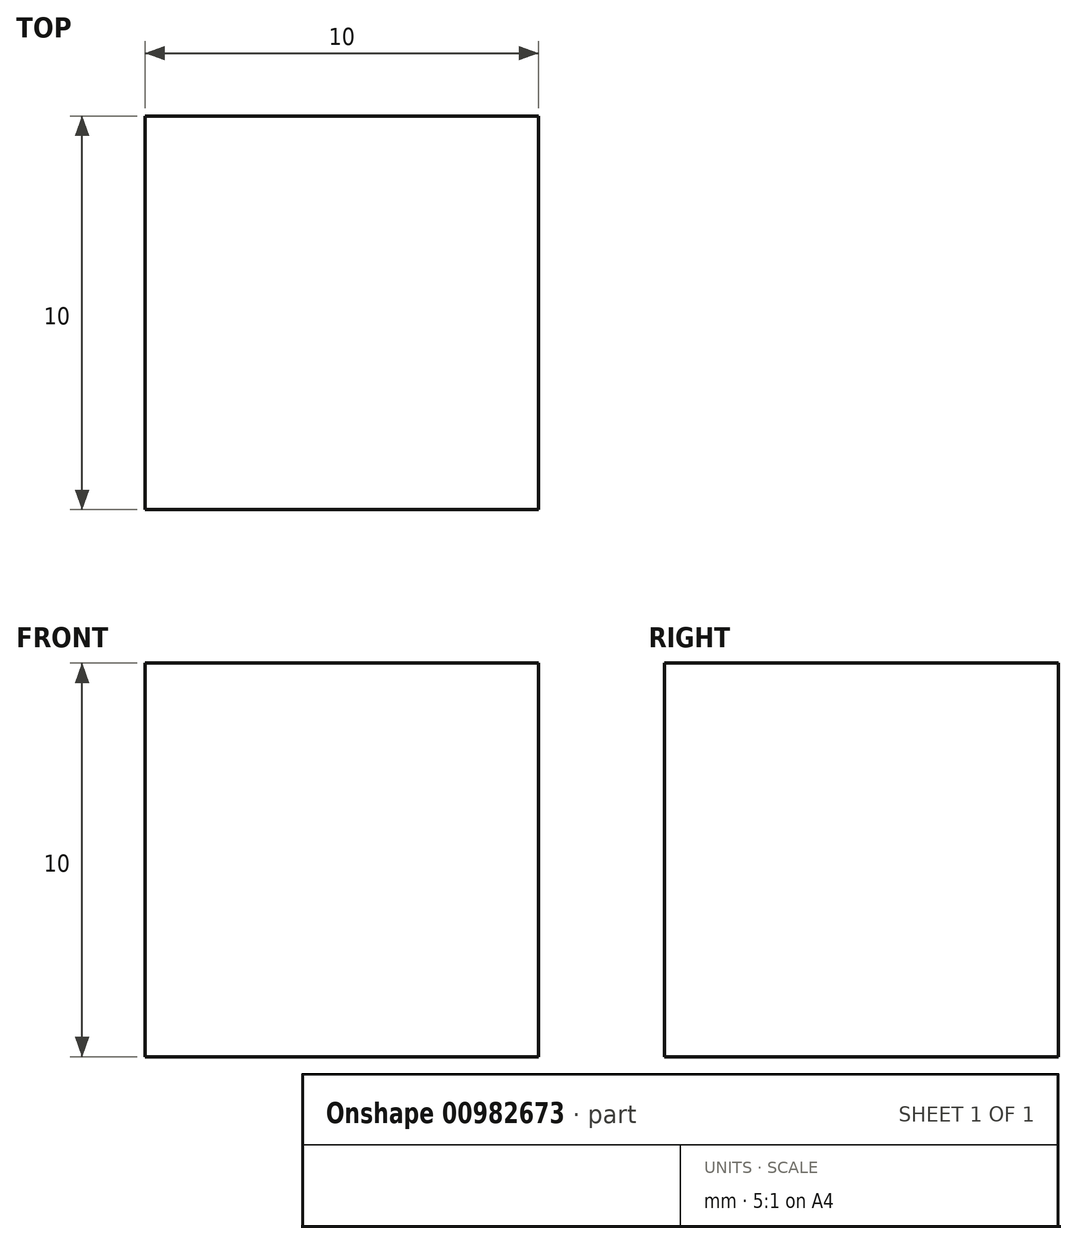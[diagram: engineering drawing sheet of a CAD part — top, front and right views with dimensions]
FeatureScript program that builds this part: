
annotation { "Feature Type Name" : "Feature", "Feature Type Description" : "" }
export const myFeature = defineFeature(function(context is Context, id is Id, definition is map)
    precondition{}
    {
        {
            var Q0;
            Q0=qCreatedBy(makeId("Front.planeOp"),FACE);
            var sketch = newSketch(context, id + "F0", { "sketchPlane" : qUnion([Q0])});
            skLineSegment(sketch, "E0.bottom", {"start": v(0, 0) * mm, "end": v(10, 0) * mm});
            skLineSegment(sketch, "E0.top", {"start": v(0, -10) * mm, "end": v(10, -10) * mm});
            skLineSegment(sketch, "E0.left", {"start": v(0, 0) * mm, "end": v(0, -10) * mm});
            skLineSegment(sketch, "E0.right", {"start": v(10, 0) * mm, "end": v(10, -10) * mm});
            skSolve(sketch);
        }
        {
            var Q0;
            Q0 = qSketchRegion(id + "F0", true);
            extrude(context, id + "F1", {"entities" : qUnion([Q0]), "depth" : 10 * mm, "offsetDistance" : 25 * mm});
        }
    });
